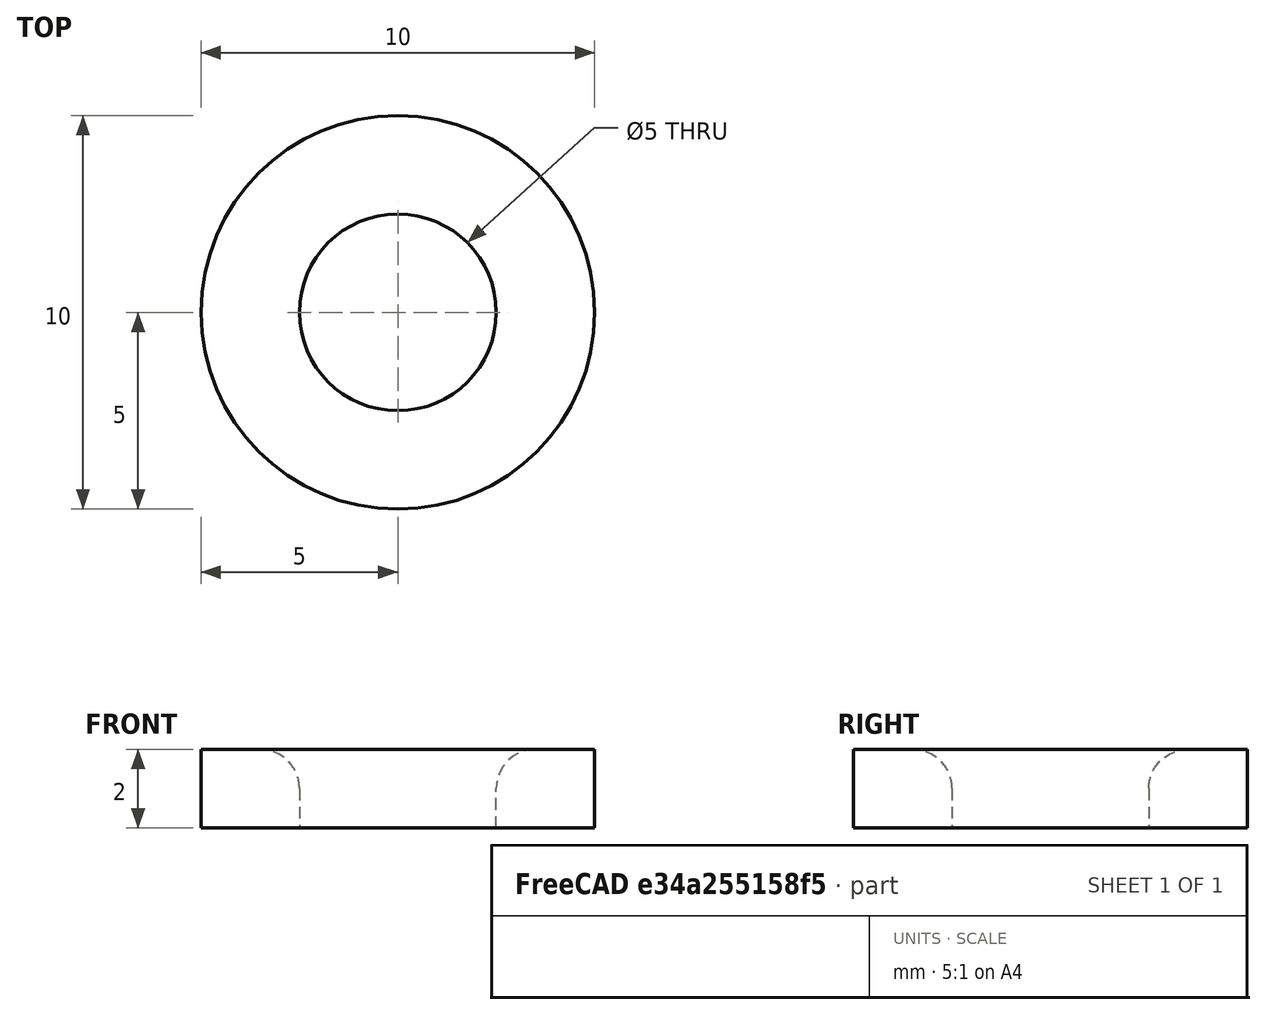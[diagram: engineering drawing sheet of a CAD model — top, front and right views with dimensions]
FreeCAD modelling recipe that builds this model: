
FCSTD DOCUMENT  (FreeCAD 2024.409R38991 (Git))
Label: Washers
License: All rights reserved
LicenseURL: https://en.wikipedia.org/wiki/All_rights_reserved
objects: Sketcher::SketchObject×1, PartDesign::Pad×1, PartDesign::Fillet×1, PartDesign::Body×1
note: 9 computed .brp shape members not serialized (recipe doc carries the construction recipe); baked Part::Feature solids carry a one-line shape summary decoded from their .brp

FEATURE [Sketcher::SketchObject] Sketch
  ArcFitTolerance = 1e-06
  AttachmentSupport = -> [XY_Plane]
  ExternalBSplineMaxDegree = 5
  ExternalBSplineTolerance = 0.0001
  FullyConstrained = true
  InternalTolerance = 1e-06
  InvalidShape = false
  MakeInternals = false
  MapMode = 5
  Support = -> [XY_Plane]
  TreeRank = 11
  ValidateShape = false
  sketch-geometry (2):
    g0: Circle CenterX=0 CenterY=0 CenterZ=0 NormalX=0 NormalY=0 NormalZ=1 AngleXU=0 Radius=5
    g1: Circle CenterX=0 CenterY=0 CenterZ=0 NormalX=0 NormalY=0 NormalZ=1 AngleXU=0 Radius=2.5
  constraints (4):
    c: Diameter(g0) = 10
    c: Diameter(g1) = 5
    c: Coincident(g1,g0)
    c: Coincident(g-1,g0)
FEATURE [PartDesign::Pad] Pad
  AddSubType = 0
  AlongSketchNormal = false
  AutoTaperInnerAngle = true
  CheckUpToFaceLimits = true
  ClaimChildren = false
  Direction = (0,0,1)
  Fit = 0
  FitJoin = 0
  InnerFit = 0
  InnerFitJoin = 0
  InvalidShape = false
  Length = 2
  Length2 = 10
  Linearize = true
  NewSolid = false
  Profile = -> Sketch
  ReferenceAxis = -> Sketch [N_Axis]
  Suppress = false
  TaperInnerAngle = 0
  TaperInnerAngleRev = 0
  TreeRank = 12
  Type = 0
  ValidateShape = true
  _ProfileBasedVersion = 1
FEATURE [PartDesign::Fillet] Fillet
  AddSubType = 0
  Base = -> Pad [Edge6]
  BaseFeature = -> Pad
  InvalidShape = false
  NewSolid = false
  Radius = 1
  SupportTransform = false
  Suppress = false
  TreeRank = 13
  UseAllEdges = false
  ValidateShape = true
FEATURE [PartDesign::Body] Body
  AutoGroupSolids = false
  ClaimAllChildren = false
  ExportMode = 0
  Group = -> [Sketch,Pad,Fillet]
  InvalidShape = false
  Origin = -> Origin
  Tip = -> Fillet
  TreeRank = 10
  ValidateShape = false
  _ExportChildren = -> [Pad,Fillet]
  _GroupVersion = 1
